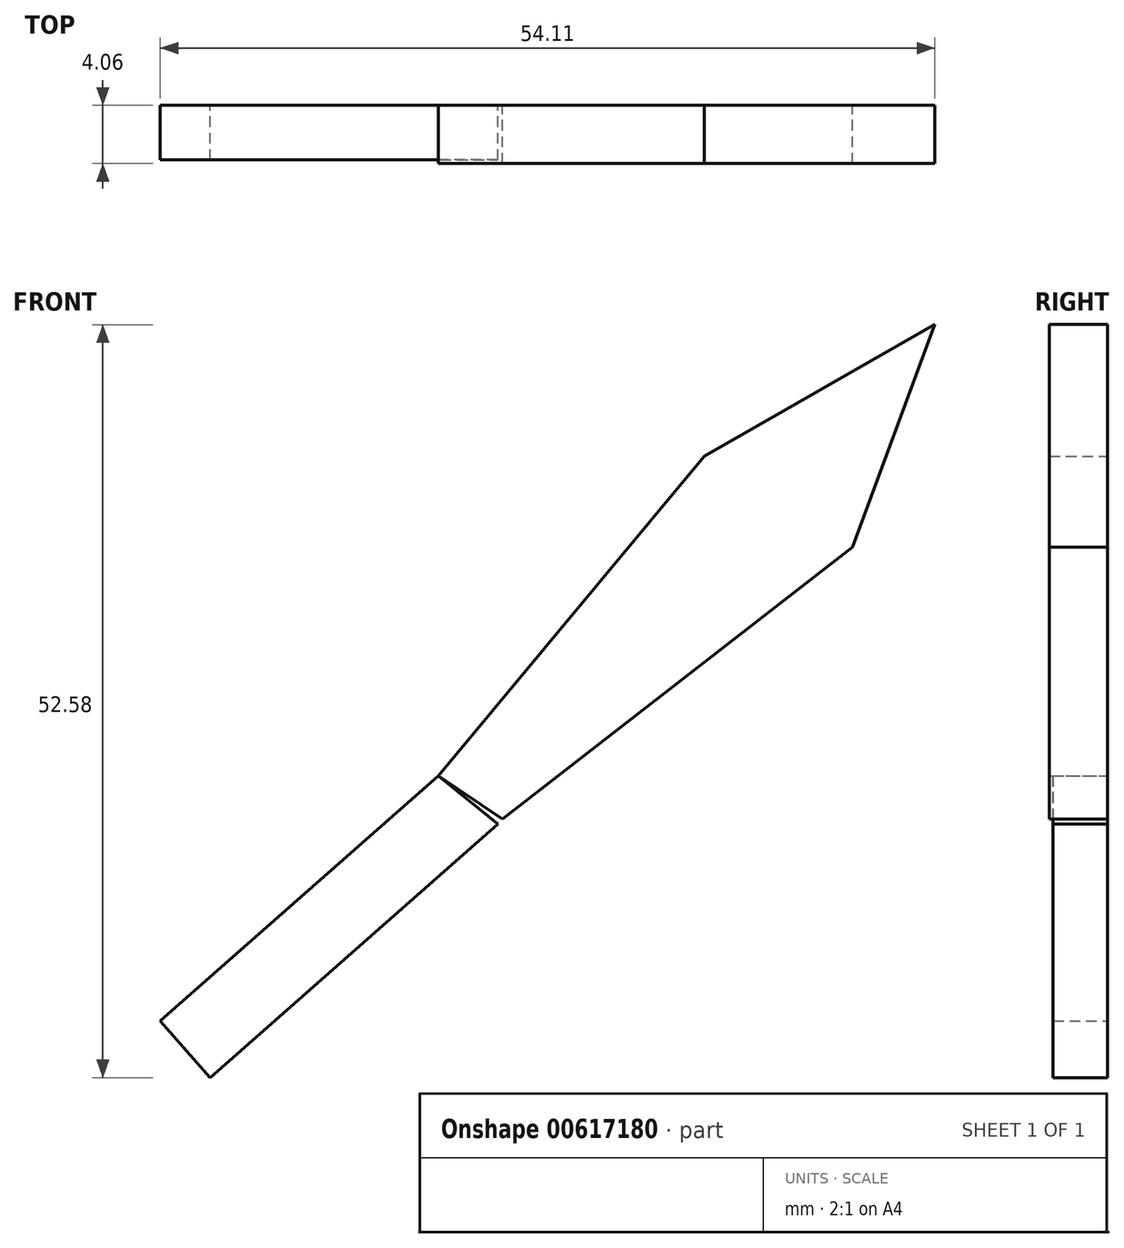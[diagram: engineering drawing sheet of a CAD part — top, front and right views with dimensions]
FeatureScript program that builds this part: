
annotation { "Feature Type Name" : "Feature", "Feature Type Description" : "" }
export const myFeature = defineFeature(function(context is Context, id is Id, definition is map)
    precondition{}
    {
        {
            var Q0;
            Q0=qCreatedBy(makeId("Front.planeOp"),FACE);
            var sketch = newSketch(context, id + "F0", { "sketchPlane" : qUnion([Q0])});
            skLineSegment(sketch, "E0", {"start": v(0, 0) * mm, "end": v(-19.43, -17.12) * mm});
            skLineSegment(sketch, "E1", {"start": v(-19.43, -17.12) * mm, "end": v(-15.95, -21.07) * mm});
            skLineSegment(sketch, "E2", {"start": v(-15.95, -21.07) * mm, "end": v(4.14, -3.35) * mm});
            skLineSegment(sketch, "E3", {"start": v(4.14, -3.35) * mm, "end": v(0, 0) * mm});
            skSolve(sketch);
        }
        {
            var Q0;
            Q0=makeQuery(id+"F0.imprint","IMPRINT",FACE,{"disambiguationData":[TD([[makeQuery(id+"F0.imprint","IMPRINT",EDGE,{"derivedFrom":sQuery(id+"F0.wireOp",EDGE,"E0")}),1.0]])]});
            extrude(context, id + "F1", {"entities" : qUnion([Q0]), "depth" : 3.8 * mm, "offsetDistance" : 25.4 * mm});
        }
        {
            var Q0;
            Q0=qCreatedBy(makeId("Front.planeOp"),FACE);
            var sketch = newSketch(context, id + "F2", { "sketchPlane" : qUnion([Q0])});
            skLineSegment(sketch, "E4", {"start": v(0, 0) * mm, "end": v(18.56, 22.3) * mm});
            skLineSegment(sketch, "E5", {"start": v(18.56, 22.3) * mm, "end": v(34.68, 31.51) * mm});
            skLineSegment(sketch, "E6", {"start": v(34.68, 31.51) * mm, "end": v(28.92, 15.97) * mm});
            skLineSegment(sketch, "E7", {"start": v(28.92, 15.97) * mm, "end": v(4.46, -3.02) * mm});
            skLineSegment(sketch, "E8", {"start": v(4.46, -3.02) * mm, "end": v(0, 0) * mm});
            skSolve(sketch);
        }
        {
            var Q0;
            Q0=makeQuery(id+"F2.imprint","IMPRINT",FACE,{"disambiguationData":[TD([[makeQuery(id+"F2.imprint","IMPRINT",EDGE,{"derivedFrom":sQuery(id+"F2.wireOp",EDGE,"E4")}),-1.0]])]});
            extrude(context, id + "F3", {"entities" : qUnion([Q0]), "depth" : 4.06 * mm, "offsetDistance" : 25.4 * mm});
        }
    });
